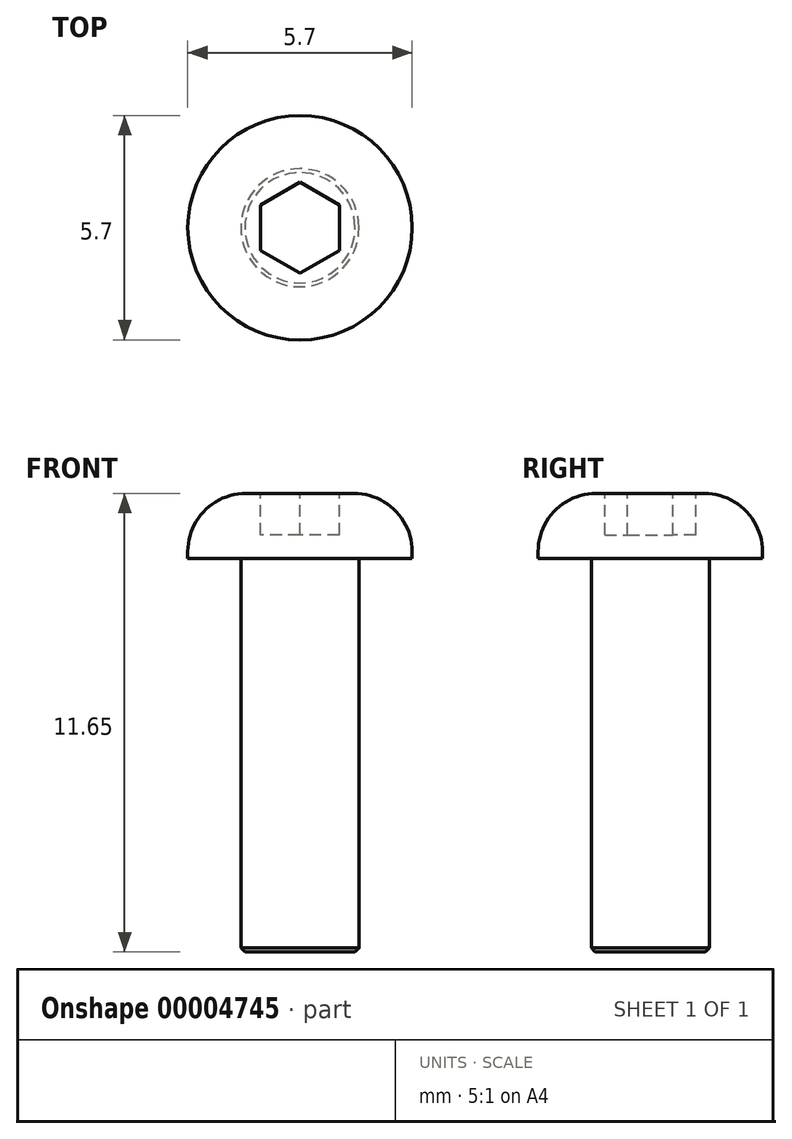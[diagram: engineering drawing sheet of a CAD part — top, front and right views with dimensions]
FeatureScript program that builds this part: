
annotation { "Feature Type Name" : "Feature", "Feature Type Description" : "" }
export const myFeature = defineFeature(function(context is Context, id is Id, definition is map)
    precondition{}
    {
        {
            var Q0;
            Q0=qCreatedBy(makeId("Top.planeOp"),FACE);
            var sketch = newSketch(context, id + "F0", { "sketchPlane" : qUnion([Q0])});
            skCircle(sketch, "E0", {"center": v(0, 0) * mm, "radius": 1.5 * mm});
            skSolve(sketch);
        }
        {
            var Q0;
            Q0=qSketchRegion(id+"F0",true);
            extrude(context, id + "F1", {"entities" : qUnion([Q0]), "oppositeDirection" : true, "depth" : 10 * mm});
        }
        {
            var Q0;
            Q0=makeQuery(id+"F1.opExtrude","CAP_EDGE",EDGE,{"disambiguationData":[OSD([sQuery(id+"F0.wireOp",EDGE,"E0")])],"isStart":false});
            chamfer(context, id + "F2", {"entities" : qUnion([Q0]), "chamferType" : ChamferType.OFFSET_ANGLE, "width" : 0.1 * mm, "oppositeDirection" : false, "angle" : 45 * degree, "tangentPropagation" : true});
        }
        {
            var Q0;
            Q0=makeQuery(id+"F1.opExtrude","CAP_FACE",FACE,{"disambiguationData":[OSD([sQuery(id+"F0.wireOp",EDGE,"E0")])],"isStart":true});
            var sketch = newSketch(context, id + "F3", { "sketchPlane" : qUnion([Q0])});
            skCircle(sketch, "E1", {"center": v(0, 0) * mm, "radius": 2.85 * mm});
            skSolve(sketch);
        }
        {
            var Q0;
            Q0=qSketchRegion(id+"F3",true);
            extrude(context, id + "F4", {"entities" : qUnion([Q0]), "operationType" : NewBodyOperationType.ADD, "depth" : 1.65 * mm});
        }
        {
            var Q0;
            Q0=makeQuery(id+"F4.opExtrude","CAP_FACE",FACE,{"disambiguationData":[OSD([sQuery(id+"F3.wireOp",EDGE,"E1")])],"isStart":false});
            var sketch = newSketch(context, id + "F5", { "sketchPlane" : qUnion([Q0])});
            skCircle(sketch, "E2.cCircle", {"center": v(0, 0) * mm, "radius": 1 * mm, "construction": true});
            skLineSegment(sketch, "E2.0", {"start": v(-1, -0.58) * mm, "end": v(-1, 0.58) * mm});
            skLineSegment(sketch, "E2.1", {"start": v(-1, 0.58) * mm, "end": v(0, 1.15) * mm});
            skLineSegment(sketch, "E2.2", {"start": v(0, 1.15) * mm, "end": v(1, 0.58) * mm});
            skLineSegment(sketch, "E2.3", {"start": v(1, 0.58) * mm, "end": v(1, -0.58) * mm});
            skLineSegment(sketch, "E2.4", {"start": v(1, -0.58) * mm, "end": v(0, -1.15) * mm});
            skLineSegment(sketch, "E2.5", {"start": v(0, -1.15) * mm, "end": v(-1, -0.58) * mm});
            skPoint(sketch, "E2.0.midPoint", {"position": v(-1, 0) * mm});
            skSolve(sketch);
        }
        {
            var Q0;
            Q0=qSketchRegion(id+"F5",true);
            extrude(context, id + "F6", {"entities" : qUnion([Q0]), "operationType" : NewBodyOperationType.REMOVE, "oppositeDirection" : true, "depth" : 1.05 * mm});
        }
        {
            var Q0;
            Q0=makeQuery(id+"F4.opExtrude","CAP_EDGE",EDGE,{"disambiguationData":[OSD([sQuery(id+"F3.wireOp",EDGE,"E1")])],"isStart":false});
            fillet(context, id + "F7", {"entities" : qUnion([Q0]), "radius" : (2.95 / 2) * mm, "tangentPropagation" : true, "allowEdgeOverflow" : false});
        }
    });
